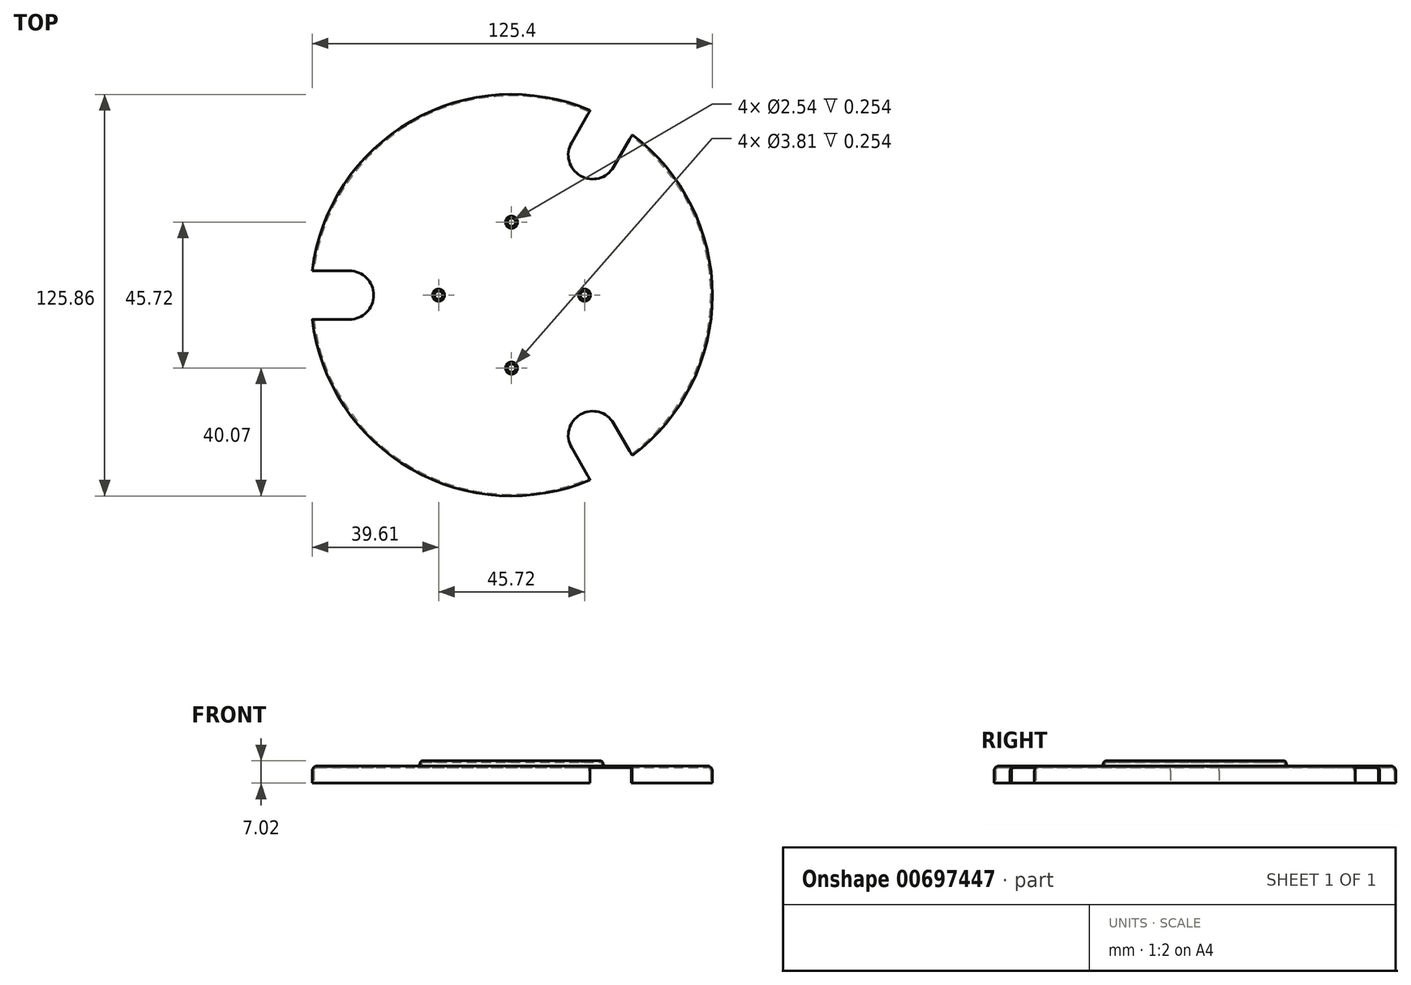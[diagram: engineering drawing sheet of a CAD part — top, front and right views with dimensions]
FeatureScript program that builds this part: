
annotation { "Feature Type Name" : "Feature", "Feature Type Description" : "" }
export const myFeature = defineFeature(function(context is Context, id is Id, definition is map)
    precondition{}
    {
        {
            var Q0;
            Q0=qCreatedBy(makeId("Front.planeOp"),FACE);
            var sketch = newSketch(context, id + "F0", { "sketchPlane" : qUnion([Q0])});
            skLineSegment(sketch, "E0", {"start": v(29.44, 34.23) * mm, "end": v(61.32, 34.23) * mm});
            skLineSegment(sketch, "E1", {"start": v(62.93, 32.62) * mm, "end": v(62.93, 28.81) * mm});
            skPoint(sketch, "E2.visualSharp", {"position": v(62.93, 34.23) * mm});
            skArc(sketch, "E2.filletArc", {"start": v(62.93, 32.62) * mm, "mid": v(62.46, 33.76) * mm, "end": v(61.32, 34.23) * mm});
            skLineSegment(sketch, "E3", {"start": v(28.7, 34.8) * mm, "end": v(28.58, 35.26) * mm});
            skLineSegment(sketch, "E4", {"start": v(27.84, 35.83) * mm, "end": v(0, 35.83) * mm});
            skPoint(sketch, "E5.visualSharp", {"position": v(28.44, 35.83) * mm});
            skArc(sketch, "E5.filletArc", {"start": v(28.58, 35.26) * mm, "mid": v(28.31, 35.67) * mm, "end": v(27.84, 35.83) * mm});
            skPoint(sketch, "E6.visualSharp", {"position": v(28.85, 34.23) * mm});
            skArc(sketch, "E6.filletArc", {"start": v(28.7, 34.8) * mm, "mid": v(28.97, 34.4) * mm, "end": v(29.44, 34.23) * mm});
            skLineSegment(sketch, "E7.0", {"start": v(27.84, 35.32) * mm, "end": v(0, 35.32) * mm});
            skArc(sketch, "E7.1", {"start": v(28.1, 35.13) * mm, "mid": v(28, 35.27) * mm, "end": v(27.84, 35.32) * mm});
            skLineSegment(sketch, "E7.2", {"start": v(28.2, 34.68) * mm, "end": v(28.1, 35.13) * mm});
            skLineSegment(sketch, "E7.3", {"start": v(62.43, 32.62) * mm, "end": v(62.43, 28.81) * mm});
            skArc(sketch, "E7.4", {"start": v(62.43, 32.62) * mm, "mid": v(62.1, 33.4) * mm, "end": v(61.32, 33.73) * mm});
            skLineSegment(sketch, "E7.5", {"start": v(29.44, 33.73) * mm, "end": v(61.32, 33.73) * mm});
            skArc(sketch, "E7.6", {"start": v(28.2, 34.68) * mm, "mid": v(28.66, 34) * mm, "end": v(29.44, 33.73) * mm});
            skLineSegment(sketch, "E8", {"start": v(62.43, 28.81) * mm, "end": v(62.93, 28.81) * mm});
            skLineSegment(sketch, "E9", {"start": v(0, 35.83) * mm, "end": v(0, 35.32) * mm});
            skSolve(sketch);
        }
        {
            var Q0;
            Q0=qCreatedBy(makeId("Front.planeOp"),FACE);
            var sketch = newSketch(context, id + "F1", { "sketchPlane" : qUnion([Q0])});
            skLineSegment(sketch, "E10", {"start": v(0, 0) * mm, "end": v(0, 107.08) * mm, "construction": true});
            skSolve(sketch);
        }
        {
            var Q0;
            Q0 = qSketchRegion(id + "F0", true);
            var Q1;
            Q1=sQuery(id+"F1.wireOp",EDGE,"E10");
            revolve(context, id + "F2", {"entities" : qUnion([Q0]), "axis" : qUnion([Q1]), "revolveType" : RevolveType.FULL});
        }
        {
            var Q0;
            Q0=makeQuery(id+"F2.opRevolve","SWEPT_FACE",FACE,{"disambiguationData":[OSD([sQuery(id+"F0.wireOp",EDGE,"E4")])]});
            var sketch = newSketch(context, id + "F3", { "sketchPlane" : qUnion([Q0])});
            skCircle(sketch, "E11", {"center": v(22.86, 0) * mm, "radius": 1.27 * mm});
            skCircle(sketch, "E12.1.0", {"center": v(0, 22.86) * mm, "radius": 1.27 * mm});
            skCircle(sketch, "E12.2.0", {"center": v(-22.86, 0) * mm, "radius": 1.27 * mm});
            skCircle(sketch, "E12.3.0", {"center": v(0, -22.86) * mm, "radius": 1.27 * mm});
            skPoint(sketch, "E12.center", {"position": v(0, 0) * mm});
            skSolve(sketch);
        }
        {
            var Q0;
            Q0=sQuery(id+"F3.wireOp",VERTEX,"E12.1.0.center");
            var Q1;
            Q1=sQuery(id+"F3.wireOp",VERTEX,"E12.2.0.center");
            var Q2;
            Q2=sQuery(id+"F3.wireOp",VERTEX,"E12.3.0.center");
            var Q3;
            Q3=sQuery(id+"F3.wireOp",VERTEX,"E11.center");
            var Q4;
            Q4=makeQuery(id+"F2.opRevolve","SWEPT_BODY",BODY,{"disambiguationData":[OSD([sQuery(id+"F0.wireOp",EDGE,"E0"),sQuery(id+"F0.wireOp",EDGE,"E1"),sQuery(id+"F0.wireOp",EDGE,"E2.filletArc"),sQuery(id+"F0.wireOp",EDGE,"E3"),sQuery(id+"F0.wireOp",EDGE,"E4"),sQuery(id+"F0.wireOp",EDGE,"E5.filletArc"),sQuery(id+"F0.wireOp",EDGE,"E6.filletArc"),sQuery(id+"F0.wireOp",EDGE,"E7.0"),sQuery(id+"F0.wireOp",EDGE,"E7.1"),sQuery(id+"F0.wireOp",EDGE,"E7.2"),sQuery(id+"F0.wireOp",EDGE,"E7.3"),sQuery(id+"F0.wireOp",EDGE,"E7.4"),sQuery(id+"F0.wireOp",EDGE,"E7.5"),sQuery(id+"F0.wireOp",EDGE,"E7.6"),sQuery(id+"F0.wireOp",EDGE,"E8"),sQuery(id+"F0.wireOp",EDGE,"E9")])]});
            hole(context, id + "F4", {"style" : HoleStyle.C_BORE, "endStyle" : HoleEndStyle.THROUGH, "holeDiameter" : 2.54 * mm, "cBoreDiameter" : 3.8 * mm, "cBoreDepth" : 0.25 * mm, "majorDiameter" : 6.35 * mm, "isTappedThrough" : true, "tappedDepth" : 12.7 * mm, "tapClearance" : 3, "locations" : qUnion([Q0, Q1, Q2, Q3]), "scope" : qUnion([Q4])});
        }
        {
            var Q0;
            Q0=makeQuery(id+"F2.opRevolve","SWEPT_FACE",FACE,{"disambiguationData":[OSD([sQuery(id+"F0.wireOp",EDGE,"E0")])]});
            var sketch = newSketch(context, id + "F5", { "sketchPlane" : qUnion([Q0])});
            skArc(sketch, "E13", {"start": v(-50.8, -7.62) * mm, "mid": v(-43.18, 0) * mm, "end": v(-50.8, 7.62) * mm});
            skLineSegment(sketch, "E14", {"start": v(0, 0) * mm, "end": v(-109.57, 0) * mm});
            skPoint(sketch, "E15", {"position": v(-50.8, 7.62) * mm});
            skPoint(sketch, "E16", {"position": v(-50.8, -7.62) * mm});
            skLineSegment(sketch, "E17", {"start": v(-50.8, 7.62) * mm, "end": v(-77.92, 7.62) * mm});
            skLineSegment(sketch, "E18", {"start": v(-50.8, -7.62) * mm, "end": v(-77.92, -7.62) * mm});
            skLineSegment(sketch, "E19", {"start": v(-77.92, 7.62) * mm, "end": v(-77.92, -7.62) * mm});
            skLineSegment(sketch, "E20.1.0", {"start": v(18.8, -47.8) * mm, "end": v(32.36, -71.3) * mm});
            skLineSegment(sketch, "E20.1.1", {"start": v(32.36, -71.3) * mm, "end": v(45.56, -63.67) * mm});
            skArc(sketch, "E20.1.2", {"start": v(32, -40.18) * mm, "mid": v(21.59, -37.4) * mm, "end": v(18.8, -47.8) * mm});
            skLineSegment(sketch, "E20.1.3", {"start": v(32, -40.18) * mm, "end": v(45.56, -63.67) * mm});
            skLineSegment(sketch, "E20.2.0", {"start": v(32, 40.18) * mm, "end": v(45.56, 63.67) * mm});
            skLineSegment(sketch, "E20.2.1", {"start": v(45.56, 63.67) * mm, "end": v(32.36, 71.3) * mm});
            skArc(sketch, "E20.2.2", {"start": v(18.8, 47.8) * mm, "mid": v(21.6, 37.4) * mm, "end": v(32, 40.18) * mm});
            skLineSegment(sketch, "E20.2.3", {"start": v(18.8, 47.8) * mm, "end": v(32.36, 71.3) * mm});
            skPoint(sketch, "E20.center", {"position": v(0, 0) * mm});
            skSolve(sketch);
        }
        {
            var Q0;
            {var subQ0=sQuery(id+"F5.wireOp",EDGE,"E19");var subQ5=sQuery(id+"F5.wireOp",EDGE,"E17");var subQ6=makeQuery(id+"F5.imprint","INTERSECT",VERTEX,{"derivedFrom":[subQ5,subQ0]});Q0=makeQuery(id+"F5.imprint","IMPRINT",FACE,{"disambiguationData":[TD([[makeQuery(id+"F5.imprint","IMPRINT",EDGE,{"disambiguationData":[TD([[subQ6,-1.0]])],"derivedFrom":subQ0}),1.0]])]});}
            var Q1;
            {var subQ0=sQuery(id+"F5.wireOp",EDGE,"E19");var subQ5=sQuery(id+"F5.wireOp",EDGE,"E18");var subQ7=makeQuery(id+"F5.imprint","INTERSECT",VERTEX,{"derivedFrom":[subQ5,subQ0]});Q1=makeQuery(id+"F5.imprint","IMPRINT",FACE,{"disambiguationData":[TD([[makeQuery(id+"F5.imprint","IMPRINT",EDGE,{"disambiguationData":[TD([[subQ7,1.0]])],"derivedFrom":subQ0}),1.0]])]});}
            var Q2;
            {var subQ0=sQuery(id+"F5.wireOp",EDGE,"E18");var subQ1=sQuery(id+"F5.wireOp",EDGE,"E13");var subQ2=makeQuery(id+"F5.imprint","INTERSECT",VERTEX,{"derivedFrom":[subQ1,subQ0]});Q2=makeQuery(id+"F5.imprint","IMPRINT",FACE,{"disambiguationData":[TD([[makeQuery(id+"F5.imprint","IMPRINT",EDGE,{"disambiguationData":[TD([[subQ2,-1.0]])],"derivedFrom":subQ1}),1.0]])]});}
            var Q3;
            {var subQ0=sQuery(id+"F5.wireOp",EDGE,"E17");var subQ1=sQuery(id+"F5.wireOp",EDGE,"E13");var subQ2=makeQuery(id+"F5.imprint","INTERSECT",VERTEX,{"derivedFrom":[subQ1,subQ0]});Q3=makeQuery(id+"F5.imprint","IMPRINT",FACE,{"disambiguationData":[TD([[makeQuery(id+"F5.imprint","IMPRINT",EDGE,{"disambiguationData":[TD([[subQ2,1.0]])],"derivedFrom":subQ1}),1.0]])]});}
            var Q4;
            {var subQ0=sQuery(id+"F5.wireOp",EDGE,"E20.2.1");Q4=makeQuery(id+"F5.imprint","IMPRINT",FACE,{"disambiguationData":[TD([[makeQuery(id+"F5.imprint","IMPRINT",EDGE,{"derivedFrom":subQ0}),1.0]])]});}
            var Q5;
            {var subQ0=sQuery(id+"F5.wireOp",EDGE,"E20.2.2");Q5=makeQuery(id+"F5.imprint","IMPRINT",FACE,{"disambiguationData":[TD([[makeQuery(id+"F5.imprint","IMPRINT",EDGE,{"derivedFrom":subQ0}),1.0]])]});}
            var Q6;
            {var subQ0=sQuery(id+"F5.wireOp",EDGE,"E20.1.2");Q6=makeQuery(id+"F5.imprint","IMPRINT",FACE,{"disambiguationData":[TD([[makeQuery(id+"F5.imprint","IMPRINT",EDGE,{"derivedFrom":subQ0}),1.0]])]});}
            var Q7;
            {var subQ0=sQuery(id+"F5.wireOp",EDGE,"E20.1.1");Q7=makeQuery(id+"F5.imprint","IMPRINT",FACE,{"disambiguationData":[TD([[makeQuery(id+"F5.imprint","IMPRINT",EDGE,{"derivedFrom":subQ0}),1.0]])]});}
            extrude(context, id + "F6", {"entities" : qUnion([Q0, Q1, Q2, Q3, Q4, Q5, Q6, Q7]), "operationType" : NewBodyOperationType.REMOVE, "endBound" : BoundingType.SYMMETRIC, "depth" : 25.4 * mm, "offsetDistance" : 25.4 * mm});
        }
    });
